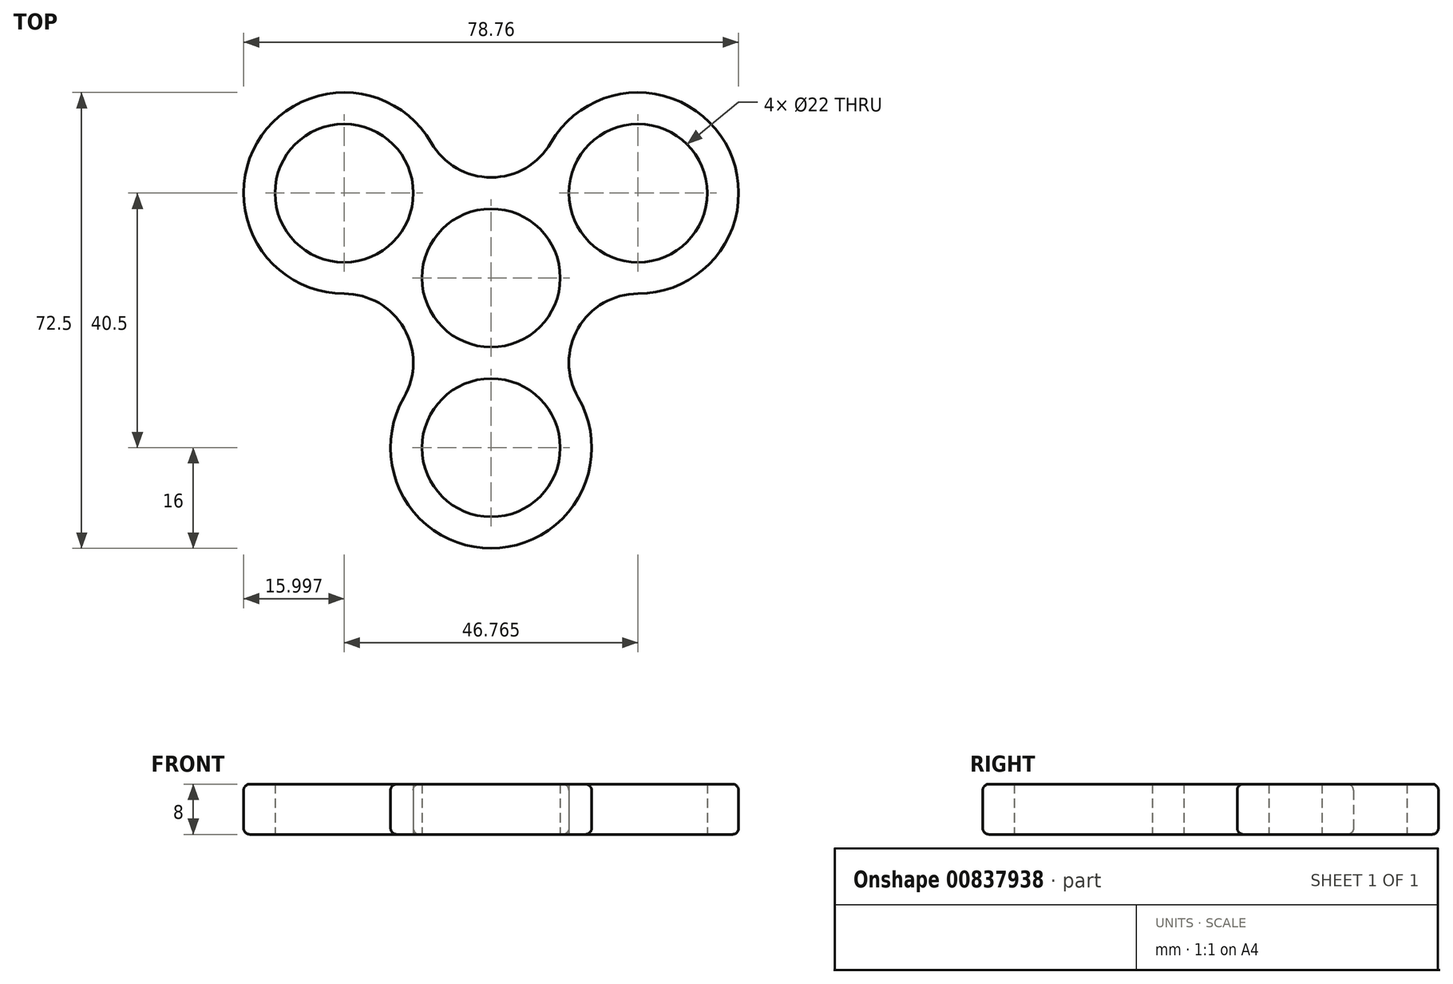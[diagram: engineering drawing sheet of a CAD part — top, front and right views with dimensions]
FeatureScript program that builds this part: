
annotation { "Feature Type Name" : "Feature", "Feature Type Description" : "" }
export const myFeature = defineFeature(function(context is Context, id is Id, definition is map)
    precondition{}
    {
        {
            var Q0;
            Q0=qCreatedBy(makeId("Top.planeOp"),FACE);
            var sketch = newSketch(context, id + "F0", { "sketchPlane" : qUnion([Q0])});
            skCircle(sketch, "E0", {"center": v(0, 0) * mm, "radius": 11 * mm});
            skCircle(sketch, "E1", {"center": v(0, -27) * mm, "radius": 11 * mm});
            skCircle(sketch, "E2", {"center": v(0, -27) * mm, "radius": 16 * mm});
            skCircle(sketch, "E3.1.0", {"center": v(23.38, -13.5) * mm, "radius": 16 * mm});
            skCircle(sketch, "E3.1.1", {"center": v(23.38, -13.5) * mm, "radius": 11 * mm});
            skCircle(sketch, "E3.2.0", {"center": v(23.38, 13.5) * mm, "radius": 16 * mm});
            skCircle(sketch, "E3.2.1", {"center": v(23.38, 13.5) * mm, "radius": 11 * mm});
            skCircle(sketch, "E3.3.0", {"center": v(0, 27) * mm, "radius": 16 * mm});
            skCircle(sketch, "E3.3.1", {"center": v(0, 27) * mm, "radius": 11 * mm});
            skCircle(sketch, "E3.4.0", {"center": v(-23.38, 13.5) * mm, "radius": 16 * mm});
            skCircle(sketch, "E3.4.1", {"center": v(-23.38, 13.5) * mm, "radius": 11 * mm});
            skCircle(sketch, "E3.5.0", {"center": v(-23.38, -13.5) * mm, "radius": 16 * mm});
            skCircle(sketch, "E3.5.1", {"center": v(-23.38, -13.5) * mm, "radius": 11 * mm});
            skSolve(sketch);
        }
        {
            var Q0;
            {var subQ0=sQuery(id+"F0.wireOp",EDGE,"E3.1.0");var subQ1=sQuery(id+"F0.wireOp",EDGE,"E1");var subQ2=makeQuery(id+"F0.imprint","INTERSECT",VERTEX,{"derivedFrom":[subQ1,subQ0]});Q0=makeQuery(id+"F0.imprint","IMPRINT",FACE,{"disambiguationData":[TD([[makeQuery(id+"F0.imprint","IMPRINT",EDGE,{"disambiguationData":[TD([[subQ2,1.0]])],"derivedFrom":subQ1}),-1.0]])]});}
            var Q1;
            {var subQ0=sQuery(id+"F0.wireOp",EDGE,"E3.5.0");var subQ1=sQuery(id+"F0.wireOp",EDGE,"E2");var subQ2=makeQuery(id+"F0.imprint","INTERSECT",VERTEX,{"disambiguationData":[OD(1.0)],"derivedFrom":[subQ1,subQ0]});Q1=makeQuery(id+"F0.imprint","IMPRINT",FACE,{"disambiguationData":[TD([[makeQuery(id+"F0.imprint","IMPRINT",EDGE,{"disambiguationData":[TD([[subQ2,-1.0]])],"derivedFrom":subQ1}),1.0]])]});}
            var Q2;
            {var subQ0=sQuery(id+"F0.wireOp",EDGE,"E3.5.0");var subQ6=sQuery(id+"F0.wireOp",EDGE,"E2");var subQ7=makeQuery(id+"F0.imprint","INTERSECT",VERTEX,{"disambiguationData":[OD(1.0)],"derivedFrom":[subQ6,subQ0]});Q2=makeQuery(id+"F0.imprint","IMPRINT",FACE,{"disambiguationData":[TD([[makeQuery(id+"F0.imprint","IMPRINT",EDGE,{"disambiguationData":[TD([[subQ7,-1.0]])],"derivedFrom":subQ6}),-1.0]])]});}
            var Q3;
            {var subQ0=sQuery(id+"F0.wireOp",EDGE,"E3.5.0");var subQ1=sQuery(id+"F0.wireOp",EDGE,"E3.4.0");var subQ2=makeQuery(id+"F0.imprint","INTERSECT",VERTEX,{"disambiguationData":[OD(1.0)],"derivedFrom":[subQ1,subQ0]});Q3=makeQuery(id+"F0.imprint","IMPRINT",FACE,{"disambiguationData":[TD([[makeQuery(id+"F0.imprint","IMPRINT",EDGE,{"disambiguationData":[TD([[subQ2,1.0]])],"derivedFrom":subQ1}),1.0]])]});}
            var Q4;
            {var subQ0=sQuery(id+"F0.wireOp",EDGE,"E3.4.0");var subQ1=sQuery(id+"F0.wireOp",EDGE,"E3.3.0");var subQ2=makeQuery(id+"F0.imprint","INTERSECT",VERTEX,{"disambiguationData":[OD(0.0)],"derivedFrom":[subQ1,subQ0]});Q4=makeQuery(id+"F0.imprint","IMPRINT",FACE,{"disambiguationData":[TD([[makeQuery(id+"F0.imprint","IMPRINT",EDGE,{"disambiguationData":[TD([[subQ2,-1.0]])],"derivedFrom":subQ1}),-1.0]])]});}
            var Q5;
            {var subQ0=sQuery(id+"F0.wireOp",EDGE,"E3.4.0");var subQ1=sQuery(id+"F0.wireOp",EDGE,"E3.3.0");var subQ2=makeQuery(id+"F0.imprint","INTERSECT",VERTEX,{"disambiguationData":[OD(1.0)],"derivedFrom":[subQ1,subQ0]});Q5=makeQuery(id+"F0.imprint","IMPRINT",FACE,{"disambiguationData":[TD([[makeQuery(id+"F0.imprint","IMPRINT",EDGE,{"disambiguationData":[TD([[subQ2,1.0]])],"derivedFrom":subQ1}),1.0]])]});}
            var Q6;
            {var subQ1=sQuery(id+"F0.wireOp",EDGE,"E3.2.0");var subQ5=sQuery(id+"F0.wireOp",EDGE,"E3.3.0");var subQ7=makeQuery(id+"F0.imprint","INTERSECT",VERTEX,{"disambiguationData":[OD(1.0)],"derivedFrom":[subQ1,subQ5]});Q6=makeQuery(id+"F0.imprint","IMPRINT",FACE,{"disambiguationData":[TD([[makeQuery(id+"F0.imprint","IMPRINT",EDGE,{"disambiguationData":[TD([[subQ7,1.0]])],"derivedFrom":subQ1}),-1.0]])]});}
            var Q7;
            {var subQ0=sQuery(id+"F0.wireOp",EDGE,"E3.3.0");var subQ1=sQuery(id+"F0.wireOp",EDGE,"E3.2.0");var subQ2=makeQuery(id+"F0.imprint","INTERSECT",VERTEX,{"disambiguationData":[OD(1.0)],"derivedFrom":[subQ1,subQ0]});Q7=makeQuery(id+"F0.imprint","IMPRINT",FACE,{"disambiguationData":[TD([[makeQuery(id+"F0.imprint","IMPRINT",EDGE,{"disambiguationData":[TD([[subQ2,1.0]])],"derivedFrom":subQ1}),1.0]])]});}
            var Q8;
            {var subQ0=sQuery(id+"F0.wireOp",EDGE,"E3.2.0");var subQ1=sQuery(id+"F0.wireOp",EDGE,"E3.1.0");var subQ2=makeQuery(id+"F0.imprint","INTERSECT",VERTEX,{"disambiguationData":[OD(0.0)],"derivedFrom":[subQ1,subQ0]});Q8=makeQuery(id+"F0.imprint","IMPRINT",FACE,{"disambiguationData":[TD([[makeQuery(id+"F0.imprint","IMPRINT",EDGE,{"disambiguationData":[TD([[subQ2,-1.0]])],"derivedFrom":subQ1}),-1.0]])]});}
            var Q9;
            {var subQ0=sQuery(id+"F0.wireOp",EDGE,"E3.2.0");var subQ1=sQuery(id+"F0.wireOp",EDGE,"E3.1.0");var subQ2=makeQuery(id+"F0.imprint","INTERSECT",VERTEX,{"disambiguationData":[OD(1.0)],"derivedFrom":[subQ1,subQ0]});Q9=makeQuery(id+"F0.imprint","IMPRINT",FACE,{"disambiguationData":[TD([[makeQuery(id+"F0.imprint","IMPRINT",EDGE,{"disambiguationData":[TD([[subQ2,1.0]])],"derivedFrom":subQ1}),1.0]])]});}
            var Q10;
            {var subQ1=sQuery(id+"F0.wireOp",EDGE,"E2");var subQ5=sQuery(id+"F0.wireOp",EDGE,"E3.1.0");var subQ7=makeQuery(id+"F0.imprint","INTERSECT",VERTEX,{"disambiguationData":[OD(1.0)],"derivedFrom":[subQ1,subQ5]});Q10=makeQuery(id+"F0.imprint","IMPRINT",FACE,{"disambiguationData":[TD([[makeQuery(id+"F0.imprint","IMPRINT",EDGE,{"disambiguationData":[TD([[subQ7,1.0]])],"derivedFrom":subQ1}),-1.0]])]});}
            var Q11;
            {var subQ0=sQuery(id+"F0.wireOp",EDGE,"E3.1.0");var subQ1=sQuery(id+"F0.wireOp",EDGE,"E2");var subQ2=makeQuery(id+"F0.imprint","INTERSECT",VERTEX,{"disambiguationData":[OD(1.0)],"derivedFrom":[subQ1,subQ0]});Q11=makeQuery(id+"F0.imprint","IMPRINT",FACE,{"disambiguationData":[TD([[makeQuery(id+"F0.imprint","IMPRINT",EDGE,{"disambiguationData":[TD([[subQ2,1.0]])],"derivedFrom":subQ1}),1.0]])]});}
            var Q12;
            {var subQ0=sQuery(id+"F0.wireOp",EDGE,"E3.1.0");var subQ1=sQuery(id+"F0.wireOp",EDGE,"E1");var subQ2=makeQuery(id+"F0.imprint","INTERSECT",VERTEX,{"derivedFrom":[subQ1,subQ0]});Q12=makeQuery(id+"F0.imprint","IMPRINT",FACE,{"disambiguationData":[TD([[makeQuery(id+"F0.imprint","IMPRINT",EDGE,{"disambiguationData":[TD([[subQ2,-1.0]])],"derivedFrom":subQ1}),-1.0]])]});}
            var Q13;
            {var subQ1=sQuery(id+"F0.wireOp",EDGE,"E3.3.0");var subQ5=sQuery(id+"F0.wireOp",EDGE,"E3.4.0");var subQ7=makeQuery(id+"F0.imprint","INTERSECT",VERTEX,{"disambiguationData":[OD(1.0)],"derivedFrom":[subQ1,subQ5]});Q13=makeQuery(id+"F0.imprint","IMPRINT",FACE,{"disambiguationData":[TD([[makeQuery(id+"F0.imprint","IMPRINT",EDGE,{"disambiguationData":[TD([[subQ7,1.0]])],"derivedFrom":subQ1}),-1.0]])]});}
            var Q14;
            {var subQ0=sQuery(id+"F0.wireOp",EDGE,"E3.4.0");var subQ1=sQuery(id+"F0.wireOp",EDGE,"E0");var subQ2=makeQuery(id+"F0.imprint","INTERSECT",VERTEX,{"derivedFrom":[subQ1,subQ0]});Q14=makeQuery(id+"F0.imprint","IMPRINT",FACE,{"disambiguationData":[TD([[makeQuery(id+"F0.imprint","IMPRINT",EDGE,{"disambiguationData":[TD([[subQ2,-1.0]])],"derivedFrom":subQ1}),-1.0]])]});}
            var Q15;
            {var subQ0=sQuery(id+"F0.wireOp",EDGE,"E3.3.0");var subQ1=sQuery(id+"F0.wireOp",EDGE,"E0");var subQ2=makeQuery(id+"F0.imprint","INTERSECT",VERTEX,{"derivedFrom":[subQ1,subQ0]});Q15=makeQuery(id+"F0.imprint","IMPRINT",FACE,{"disambiguationData":[TD([[makeQuery(id+"F0.imprint","IMPRINT",EDGE,{"disambiguationData":[TD([[subQ2,-1.0]])],"derivedFrom":subQ1}),-1.0]])]});}
            var Q16;
            {var subQ0=sQuery(id+"F0.wireOp",EDGE,"E3.3.0");var subQ1=sQuery(id+"F0.wireOp",EDGE,"E0");var subQ2=makeQuery(id+"F0.imprint","INTERSECT",VERTEX,{"derivedFrom":[subQ1,subQ0]});Q16=makeQuery(id+"F0.imprint","IMPRINT",FACE,{"disambiguationData":[TD([[makeQuery(id+"F0.imprint","IMPRINT",EDGE,{"disambiguationData":[TD([[subQ2,1.0]])],"derivedFrom":subQ1}),-1.0]])]});}
            var Q17;
            {var subQ0=sQuery(id+"F0.wireOp",EDGE,"E3.2.0");var subQ1=sQuery(id+"F0.wireOp",EDGE,"E0");var subQ2=makeQuery(id+"F0.imprint","INTERSECT",VERTEX,{"derivedFrom":[subQ1,subQ0]});Q17=makeQuery(id+"F0.imprint","IMPRINT",FACE,{"disambiguationData":[TD([[makeQuery(id+"F0.imprint","IMPRINT",EDGE,{"disambiguationData":[TD([[subQ2,1.0]])],"derivedFrom":subQ1}),-1.0]])]});}
            var Q18;
            {var subQ0=sQuery(id+"F0.wireOp",EDGE,"E2");var subQ1=sQuery(id+"F0.wireOp",EDGE,"E0");var subQ2=makeQuery(id+"F0.imprint","INTERSECT",VERTEX,{"derivedFrom":[subQ1,subQ0]});Q18=makeQuery(id+"F0.imprint","IMPRINT",FACE,{"disambiguationData":[TD([[makeQuery(id+"F0.imprint","IMPRINT",EDGE,{"disambiguationData":[TD([[subQ2,-1.0]])],"derivedFrom":subQ1}),-1.0]])]});}
            var Q19;
            {var subQ0=sQuery(id+"F0.wireOp",EDGE,"E3.5.0");var subQ1=sQuery(id+"F0.wireOp",EDGE,"E0");var subQ2=makeQuery(id+"F0.imprint","INTERSECT",VERTEX,{"derivedFrom":[subQ1,subQ0]});Q19=makeQuery(id+"F0.imprint","IMPRINT",FACE,{"disambiguationData":[TD([[makeQuery(id+"F0.imprint","IMPRINT",EDGE,{"disambiguationData":[TD([[subQ2,-1.0]])],"derivedFrom":subQ1}),-1.0]])]});}
            var Q20;
            {var subQ1=sQuery(id+"F0.wireOp",EDGE,"E3.1.0");var subQ5=sQuery(id+"F0.wireOp",EDGE,"E3.2.0");var subQ7=makeQuery(id+"F0.imprint","INTERSECT",VERTEX,{"disambiguationData":[OD(1.0)],"derivedFrom":[subQ1,subQ5]});Q20=makeQuery(id+"F0.imprint","IMPRINT",FACE,{"disambiguationData":[TD([[makeQuery(id+"F0.imprint","IMPRINT",EDGE,{"disambiguationData":[TD([[subQ7,1.0]])],"derivedFrom":subQ1}),-1.0]])]});}
            extrude(context, id + "F1", {"entities" : qUnion([Q0, Q1, Q2, Q3, Q4, Q5, Q6, Q7, Q8, Q9, Q10, Q11, Q12, Q13, Q14, Q15, Q16, Q17, Q18, Q19, Q20]), "depth" : 8 * mm, "offsetDistance" : 25 * mm});
        }
        {
            var Q0;
            Q0=makeQuery(id+"F1.opExtrude","SWEPT_FACE",FACE,{"disambiguationData":[OSD([sQuery(id+"F0.wireOp",EDGE,"E2")])]});
            fillet(context, id + "F2", {"entities" : qUnion([Q0]), "radius" : 1 * mm, "tangentPropagation" : true, "allowEdgeOverflow" : false});
        }
    });
